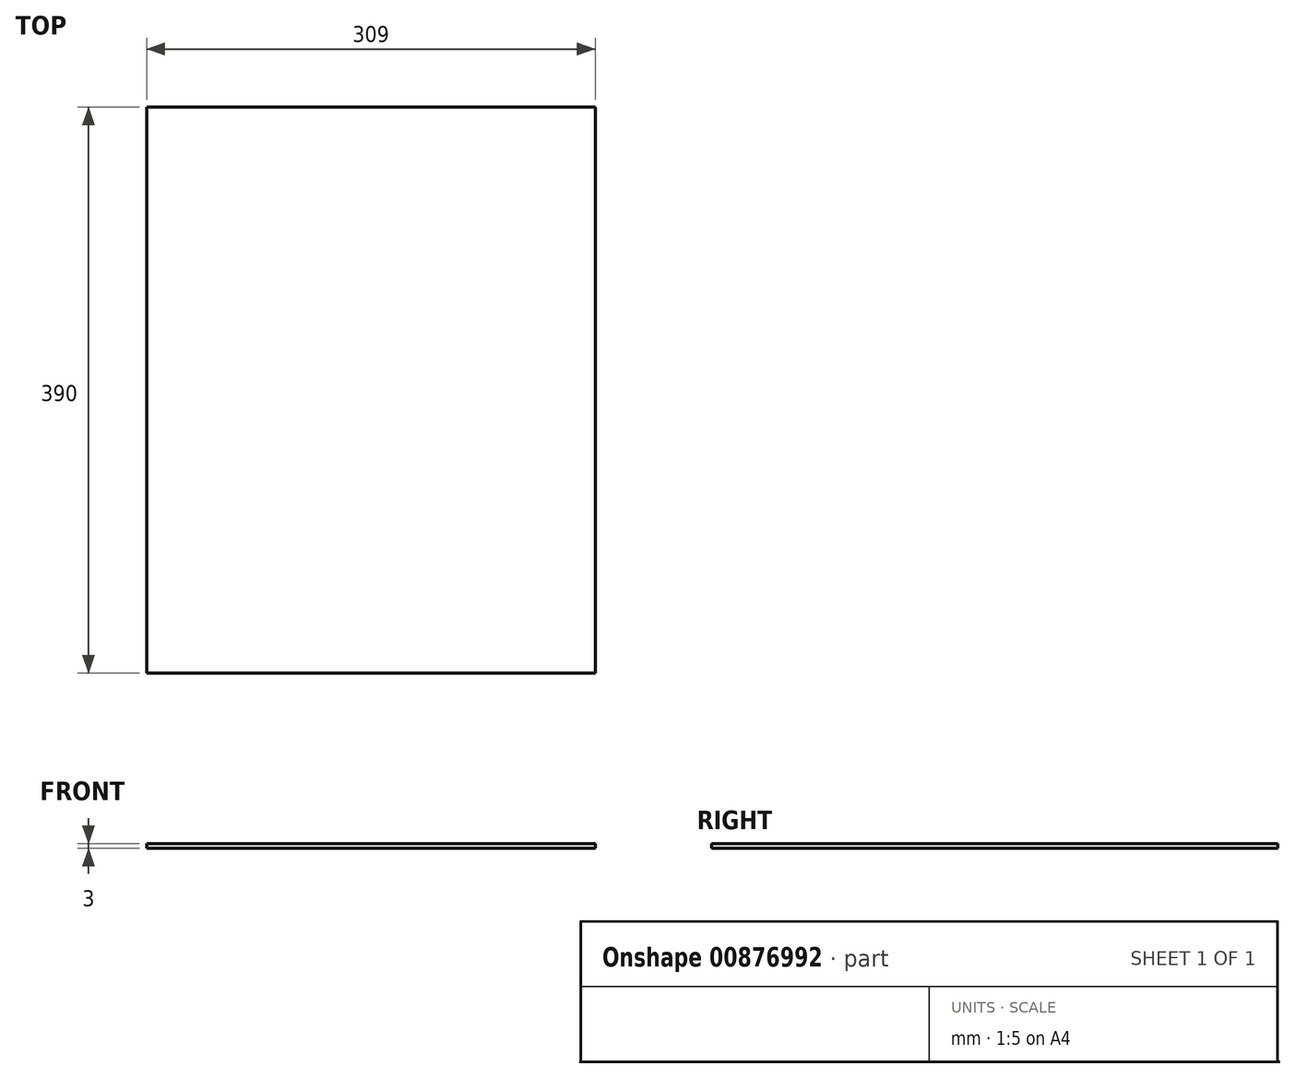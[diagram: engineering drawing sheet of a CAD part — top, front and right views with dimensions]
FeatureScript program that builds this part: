
annotation { "Feature Type Name" : "Feature", "Feature Type Description" : "" }
export const myFeature = defineFeature(function(context is Context, id is Id, definition is map)
    precondition{}
    {
        {
            var Q0;
            Q0=qCreatedBy(makeId("Top.planeOp"),FACE);
            var sketch = newSketch(context, id + "F0", { "sketchPlane" : qUnion([Q0]), "disableImprinting" : false});
            skLineSegment(sketch, "E0.bottom", {"start": v(-154.5, 195) * mm, "end": v(154.5, 195) * mm});
            skLineSegment(sketch, "E0.top", {"start": v(-154.5, -195) * mm, "end": v(154.5, -195) * mm});
            skLineSegment(sketch, "E0.left", {"start": v(-154.5, 195) * mm, "end": v(-154.5, -195) * mm});
            skLineSegment(sketch, "E0.right", {"start": v(154.5, 195) * mm, "end": v(154.5, -195) * mm});
            skPoint(sketch, "E0.middle", {"position": v(0, 0) * mm});
            skSolve(sketch);
        }
        {
            var Q0;
            Q0=makeQuery(id+"F0.imprint","IMPRINT",FACE,{"disambiguationData":[TD([[makeQuery(id+"F0.imprint","IMPRINT",EDGE,{"derivedFrom":sQuery(id+"F0.wireOp",EDGE,"E0.bottom")}),-1.0]])]});
            extrude(context, id + "F1", {"entities" : qUnion([Q0]), "depth" : 3 * mm, "offsetDistance" : 25 * mm});
        }
    });
